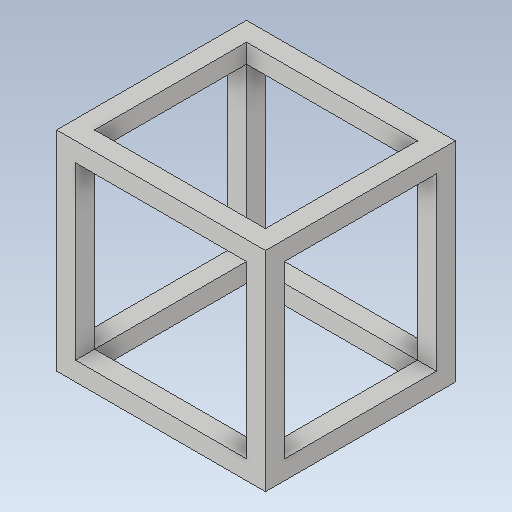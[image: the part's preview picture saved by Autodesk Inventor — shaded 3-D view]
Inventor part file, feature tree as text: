
AUTODESK INVENTOR PART (.ipt)
format: ipt  version: 2020 (Build 240168000, 168)  size: 225,280 bytes
history: native  units: mm
features: extrude x11, sketch x11
ambient origin geometry x8: Origin, YZ Plane, XZ Plane, XY Plane, X Axis, Y Axis, Z Axis, Center Point
bodies: Solid1 (feature_tree)
feature tree (22):
  extrude  "Extrusion1"  Depth=240.0mm
  extrude  "Extrusion2"  Depth=30.0mm
  extrude  "Extrusion3"  Depth=30.0mm
  extrude  "Extrusion4"  Depth=500.0mm TaperAngle=0.0deg
  extrude  "Extrusion5"  Depth=30.0mm
  extrude  "Extrusion6"  Depth=30.0mm
  extrude  "Extrusion7"  Depth=500.0mm TaperAngle=0.0deg
  extrude  "Extrusion8"  Depth=10.0mm
  extrude  "Extrusion9"  Depth=10.0mm
  extrude  "Extrusion10"  Depth=10.0mm
  extrude  "Extrusion11"  Depth=20.0mm TaperAngle=0.0deg
  sketch  "Sketch1"  dims[d0=240.0mm d1=240.0mm]
  sketch  "Sketch2"  dims[d2=240.0mm d3=0.0mm d4=30.0mm]
  sketch  "Sketch3"  dims[d5=30.0mm d6=30.0mm]
  sketch  "Sketch4"  dims[d7=30.0mm d8=500.0mm d9=0.0mm]
  sketch  "Sketch5"  dims[d10=30.0mm d11=30.0mm]
  sketch  "Sketch6"  dims[d12=30.0mm d13=30.0mm]
  sketch  "Sketch10"  dims[d14=500.0mm d15=0.0mm d16=500.0mm d17=0.0mm]
  sketch  "Sketch11"  dims[d18=10.0mm d19=10.0mm]
  sketch  "Sketch12"  dims[d20=10.0mm d21=10.0mm]
  sketch  "Sketch13"  dims[d22=900.0mm d23=0.0mm d24=10.0mm]
  sketch  "Sketch14"  dims[d25=10.0mm d26=900.0mm d27=0.0mm d29=900.0mm d30=0.0mm d31=20.0mm d32=220.0mm d33=0.0mm d34=20.0mm d35=0.0mm d36=20.0mm d37=0.0mm d38=20.0mm d39=0.0mm]
